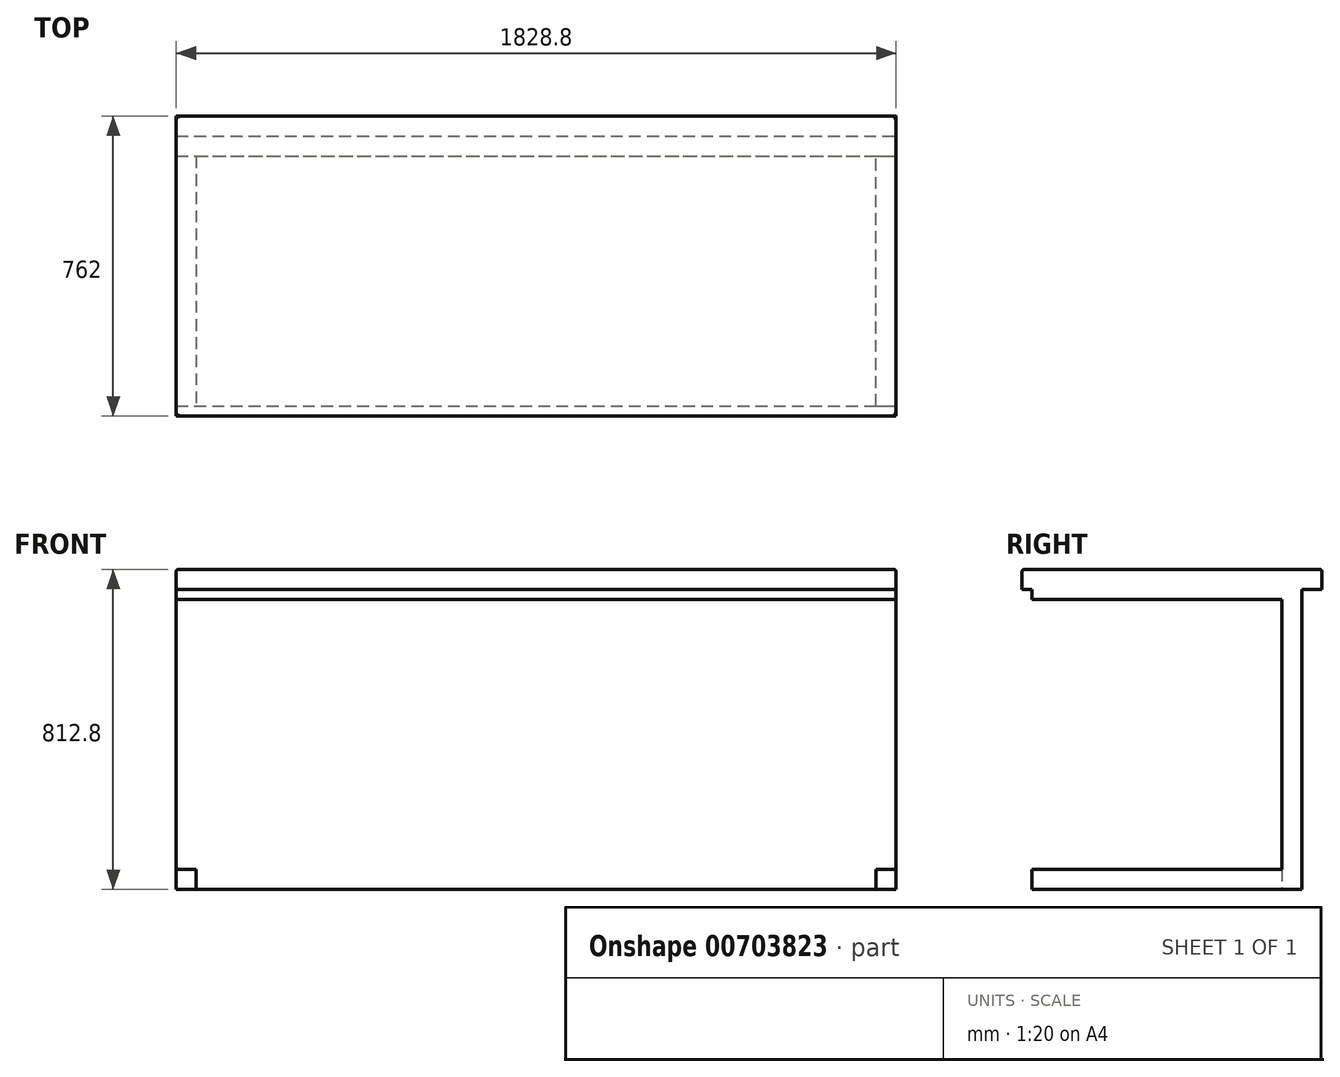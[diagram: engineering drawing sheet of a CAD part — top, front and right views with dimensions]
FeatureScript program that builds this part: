
annotation { "Feature Type Name" : "Feature", "Feature Type Description" : "" }
export const myFeature = defineFeature(function(context is Context, id is Id, definition is map)
    precondition{}
    {
        {
            var Q0;
            Q0=qCreatedBy(makeId("Top.planeOp"),FACE);
            var sketch = newSketch(context, id + "F0", { "sketchPlane" : qUnion([Q0])});
            skLineSegment(sketch, "E0.bottom", {"start": v(914.4, -381) * mm, "end": v(-914.4, -381) * mm});
            skLineSegment(sketch, "E0.top", {"start": v(914.4, 381) * mm, "end": v(-914.4, 381) * mm});
            skLineSegment(sketch, "E0.left", {"start": v(914.4, -381) * mm, "end": v(914.4, 381) * mm});
            skLineSegment(sketch, "E0.right", {"start": v(-914.4, -381) * mm, "end": v(-914.4, 381) * mm});
            skPoint(sketch, "E0.middle", {"position": v(0, 0) * mm});
            skSolve(sketch);
        }
        {
            var Q0;
            Q0=qSketchRegion(id+"F0",true);
            extrude(context, id + "F1", {"entities" : qUnion([Q0]), "depth" : 50.8 * mm, "offsetDistance" : 25.4 * mm});
        }
        {
            var Q0;
            Q0=makeQuery(id+"F1.opExtrude","CAP_FACE",FACE,{"disambiguationData":[OSD([sQuery(id+"F0.wireOp",EDGE,"E0.bottom"),sQuery(id+"F0.wireOp",EDGE,"E0.top"),sQuery(id+"F0.wireOp",EDGE,"E0.left"),sQuery(id+"F0.wireOp",EDGE,"E0.right")])],"isStart":false});
            fillet(context, id + "F2", {"entities" : qUnion([Q0]), "radius" : 5.08 * mm, "tangentPropagation" : true, "allowEdgeOverflow" : false});
        }
        {
            var Q0;
            Q0=makeQuery(id+"F1.opExtrude","SWEPT_FACE",FACE,{"disambiguationData":[OSD([sQuery(id+"F0.wireOp",EDGE,"E0.left")])]});
            var sketch = newSketch(context, id + "F3", { "sketchPlane" : qUnion([Q0])});
            skLineSegment(sketch, "E1", {"start": v(330.2, 0) * mm, "end": v(330.2, -762) * mm});
            skLineSegment(sketch, "E2", {"start": v(330.2, -762) * mm, "end": v(-355.6, -762) * mm});
            skLineSegment(sketch, "E3", {"start": v(-355.6, -762) * mm, "end": v(-355.6, -711.2) * mm});
            skLineSegment(sketch, "E4", {"start": v(-355.6, -711.2) * mm, "end": v(279.4, -711.2) * mm});
            skLineSegment(sketch, "E5", {"start": v(279.4, -711.2) * mm, "end": v(279.4, -25.4) * mm});
            skLineSegment(sketch, "E6", {"start": v(279.4, -25.4) * mm, "end": v(-355.6, -25.4) * mm});
            skLineSegment(sketch, "E7", {"start": v(-355.6, -25.4) * mm, "end": v(-355.6, 0) * mm});
            skLineSegment(sketch, "E8", {"start": v(-355.6, 0) * mm, "end": v(330.2, 0) * mm});
            skSolve(sketch);
        }
        {
            var Q0;
            Q0=qSketchRegion(id+"F3",true);
            extrude(context, id + "F4", {"entities" : qUnion([Q0]), "operationType" : NewBodyOperationType.ADD, "oppositeDirection" : true, "depth" : 1828.8 * mm, "offsetDistance" : 25.4 * mm});
        }
        {
            var Q0;
            Q0=makeQuery(id+"F4.opExtrude","SWEPT_FACE",FACE,{"disambiguationData":[OSD([sQuery(id+"F3.wireOp",EDGE,"E2")])]});
            var sketch = newSketch(context, id + "F5", { "sketchPlane" : qUnion([Q0])});
            skLineSegment(sketch, "E9.bottom", {"start": v(-863.6, 355.6) * mm, "end": v(863.6, 355.6) * mm});
            skLineSegment(sketch, "E9.top", {"start": v(-863.6, -279.4) * mm, "end": v(863.6, -279.4) * mm});
            skLineSegment(sketch, "E9.left", {"start": v(-863.6, 355.6) * mm, "end": v(-863.6, -279.4) * mm});
            skLineSegment(sketch, "E9.right", {"start": v(863.6, 355.6) * mm, "end": v(863.6, -279.4) * mm});
            skSolve(sketch);
        }
        {
            var Q0;
            Q0=qSketchRegion(id+"F5",true);
            extrude(context, id + "F6", {"entities" : qUnion([Q0]), "operationType" : NewBodyOperationType.REMOVE, "endBound" : BoundingType.UP_TO_NEXT, "oppositeDirection" : true, "depth" : 25.4 * mm, "offsetDistance" : 25.4 * mm});
        }
    });
